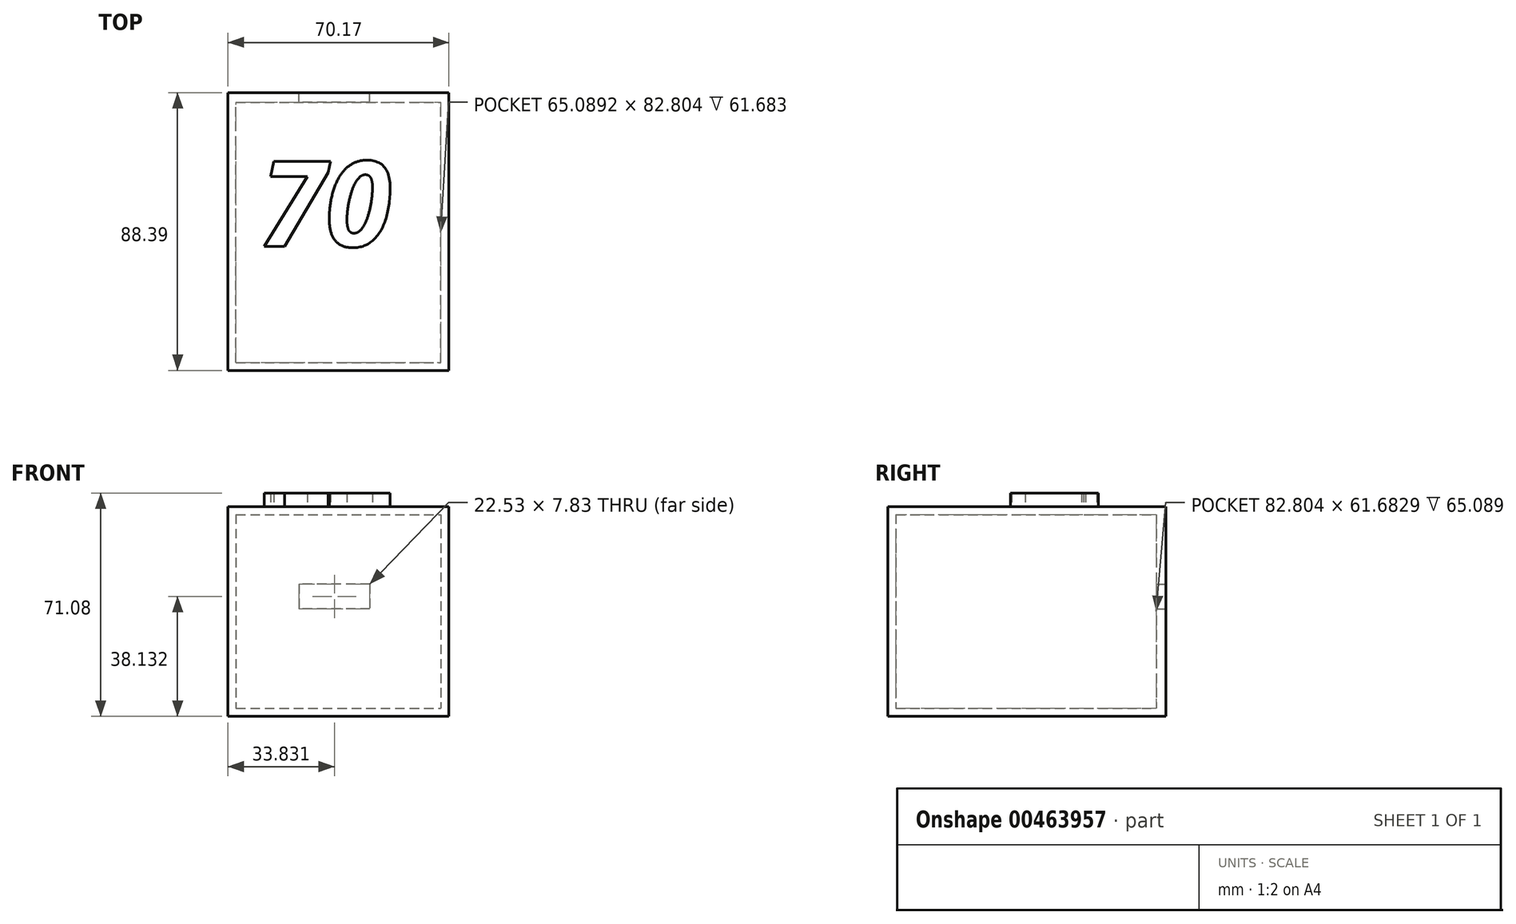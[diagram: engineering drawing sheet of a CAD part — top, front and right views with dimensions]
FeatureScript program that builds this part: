
annotation { "Feature Type Name" : "Feature", "Feature Type Description" : "" }
export const myFeature = defineFeature(function(context is Context, id is Id, definition is map)
    precondition{}
    {
        {
            var Q0;
            Q0=qCreatedBy(makeId("Front.planeOp"),FACE);
            var sketch = newSketch(context, id + "F0", { "sketchPlane" : qUnion([Q0])});
            skLineSegment(sketch, "E0.bottom", {"start": v(-31.73, 52.02) * mm, "end": v(38.44, 52.02) * mm});
            skLineSegment(sketch, "E0.top", {"start": v(-31.73, -14.74) * mm, "end": v(38.44, -14.74) * mm});
            skLineSegment(sketch, "E0.left", {"start": v(-31.73, 52.02) * mm, "end": v(-31.73, -14.74) * mm});
            skLineSegment(sketch, "E0.right", {"start": v(38.44, 52.02) * mm, "end": v(38.44, -14.74) * mm});
            skSolve(sketch);
        }
        {
            var Q0;
            Q0=makeQuery(id+"F0.imprint","IMPRINT",FACE,{"disambiguationData":[TD([[makeQuery(id+"F0.imprint","IMPRINT",EDGE,{"derivedFrom":sQuery(id+"F0.wireOp",EDGE,"E0.bottom")}),-1.0]])]});
            extrude(context, id + "F1", {"entities" : qUnion([Q0]), "depth" : 59.94 * mm});
        }
        {
            var Q0;
            Q0=makeQuery(id+"F1.opExtrude","CAP_FACE",FACE,{"disambiguationData":[OSD([sQuery(id+"F0.wireOp",EDGE,"E0.bottom"),sQuery(id+"F0.wireOp",EDGE,"E0.top"),sQuery(id+"F0.wireOp",EDGE,"E0.left"),sQuery(id+"F0.wireOp",EDGE,"E0.right")])],"isStart":true});
            var sketch = newSketch(context, id + "F2", { "sketchPlane" : qUnion([Q0])});
            skSolve(sketch);
        }
        {
            var Q0;
            Q0=makeQuery(id+"F2.imprint","IMPRINT",FACE,{"disambiguationData":[TD([[makeQuery(id+"F2.imprint","IMPRINT",EDGE,{"derivedFrom":makeQuery(id+"F1.opExtrude","CAP_EDGE",EDGE,{"disambiguationData":[OSD([sQuery(id+"F0.wireOp",EDGE,"E0.bottom")])],"isStart":true})}),1.0]])]});
            extrude(context, id + "F3", {"entities" : qUnion([Q0]), "operationType" : NewBodyOperationType.ADD, "depth" : 25.4 * mm});
        }
        {
            var Q0;
            Q0=makeQuery(id+"F3.opExtrude","CAP_FACE",FACE,{"disambiguationData":[OSD([sQuery(id+"F0.wireOp",EDGE,"E0.bottom"),sQuery(id+"F0.wireOp",EDGE,"E0.top"),sQuery(id+"F0.wireOp",EDGE,"E0.left"),sQuery(id+"F0.wireOp",EDGE,"E0.right")])],"isStart":false});
            shell(context, id + "F4", {"entities" : qUnion([Q0]), "thickness" : 2.54 * mm});
        }
        {
            var Q0;
            Q0=makeQuery(id+"F3.opExtrude","CAP_FACE",FACE,{"disambiguationData":[OSD([sQuery(id+"F0.wireOp",EDGE,"E0.bottom"),sQuery(id+"F0.wireOp",EDGE,"E0.top"),sQuery(id+"F0.wireOp",EDGE,"E0.left"),sQuery(id+"F0.wireOp",EDGE,"E0.right")])],"isStart":false});
            var sketch = newSketch(context, id + "F5", { "sketchPlane" : qUnion([Q0])});
            skLineSegment(sketch, "E1.0", {"start": v(31.73, 52.02) * mm, "end": v(-38.44, 52.02) * mm});
            skLineSegment(sketch, "E1.1", {"start": v(-38.44, 52.02) * mm, "end": v(-38.44, -14.74) * mm});
            skLineSegment(sketch, "E1.2", {"start": v(31.73, -14.74) * mm, "end": v(-38.44, -14.74) * mm});
            skLineSegment(sketch, "E1.3", {"start": v(31.73, 52.02) * mm, "end": v(31.73, -14.74) * mm});
            skSolve(sketch);
        }
        {
            var Q0;
            Q0 = qSketchRegion(id + "F5", true);
            extrude(context, id + "F6", {"entities" : qUnion([Q0]), "operationType" : NewBodyOperationType.ADD, "depth" : 3.05 * mm});
        }
        {
            var Q0;
            Q0=makeQuery(id+"F6.opExtrude","CAP_FACE",FACE,{"disambiguationData":[OSD([sQuery(id+"F5.wireOp",EDGE,"E1.0"),sQuery(id+"F5.wireOp",EDGE,"E1.1"),sQuery(id+"F5.wireOp",EDGE,"E1.2"),sQuery(id+"F5.wireOp",EDGE,"E1.3")])],"isStart":false});
            var sketch = newSketch(context, id + "F7", { "sketchPlane" : qUnion([Q0])});
            skSolve(sketch);
        }
        {
            var Q0;
            Q0=makeQuery(id+"F7.imprint","IMPRINT",FACE,{"disambiguationData":[TD([[makeQuery(id+"F7.imprint","IMPRINT",EDGE,{"derivedFrom":makeQuery(id+"F6.opExtrude","CAP_EDGE",EDGE,{"disambiguationData":[OSD([sQuery(id+"F5.wireOp",EDGE,"E1.0")])],"isStart":false})}),1.0]])]});
            var sketch = newSketch(context, id + "F8", { "sketchPlane" : qUnion([Q0])});
            skLineSegment(sketch, "E2.bottom", {"start": v(-13.37, 27.3) * mm, "end": v(9.17, 27.3) * mm});
            skLineSegment(sketch, "E2.top", {"start": v(-13.37, 19.48) * mm, "end": v(9.17, 19.48) * mm});
            skLineSegment(sketch, "E2.left", {"start": v(-13.37, 27.3) * mm, "end": v(-13.37, 19.48) * mm});
            skLineSegment(sketch, "E2.right", {"start": v(9.17, 27.3) * mm, "end": v(9.17, 19.48) * mm});
            skSolve(sketch);
        }
        {
            var Q0;
            Q0 = qSketchRegion(id + "F8", true);
            extrude(context, id + "F9", {"entities" : qUnion([Q0]), "operationType" : NewBodyOperationType.REMOVE, "oppositeDirection" : true, "depth" : 15.24 * mm});
        }
        {
            var Q0;
            {var subQ0=sQuery(id+"F0.wireOp",EDGE,"E0.bottom");Q0=makeQuery(id+"F6.boolean.opBoolean","MERGE",FACE,{"derivedFrom":[makeQuery(id+"F3.boolean.opBoolean","MERGE",FACE,{"derivedFrom":[makeQuery(id+"F1.opExtrude","SWEPT_FACE",FACE,{"disambiguationData":[OSD([subQ0])]}),makeQuery(id+"F3.opExtrude","SWEPT_FACE",FACE,{"disambiguationData":[OSD([subQ0])]})]}),makeQuery(id+"F6.opExtrude","SWEPT_FACE",FACE,{"disambiguationData":[OSD([sQuery(id+"F5.wireOp",EDGE,"E1.0")])]})]});}
            var sketch = newSketch(context, id + "F10", { "sketchPlane" : qUnion([Q0])});
            skText(sketch, "E3", { "text": "70", "fontName": "OpenSans-BoldItalic.ttf"});
            const initialGuessF10  = {"E3": [-0.02164, -0.02055, 1, 0, 0.0273]};
            skSetInitialGuess(sketch, initialGuessF10);
            skSolve(sketch);
        }
        {
            var Q0;
            Q0 = qSketchRegion(id + "F10", true);
            extrude(context, id + "F11", {"entities" : qUnion([Q0]), "operationType" : NewBodyOperationType.ADD, "depth" : 4.32 * mm});
        }
    });
